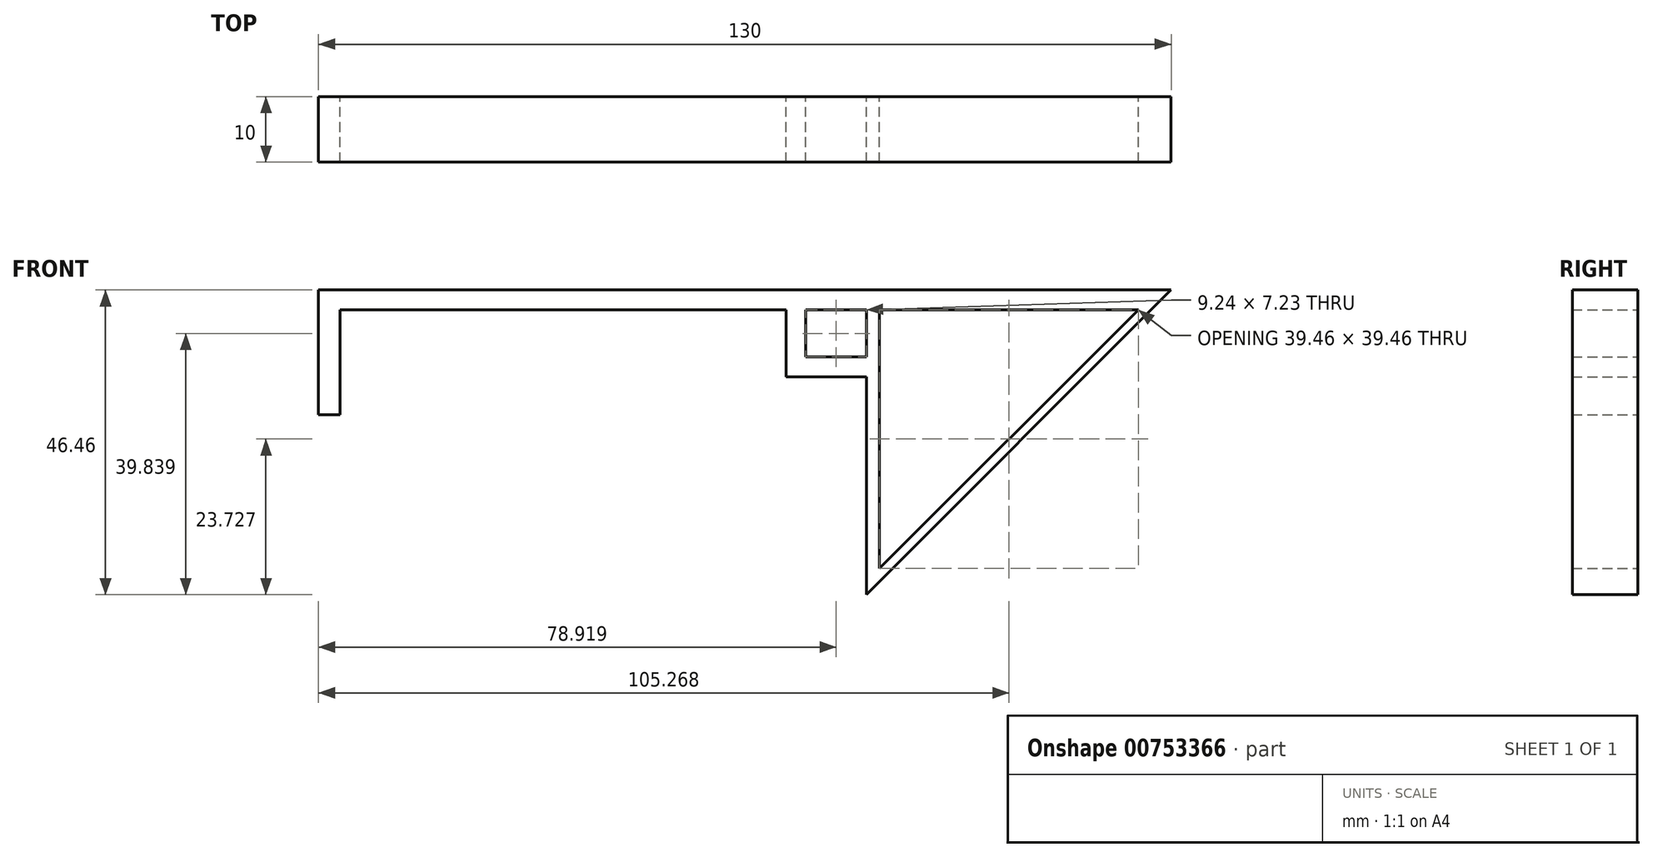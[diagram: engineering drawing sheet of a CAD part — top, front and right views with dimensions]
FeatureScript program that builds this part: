
annotation { "Feature Type Name" : "Feature", "Feature Type Description" : "" }
export const myFeature = defineFeature(function(context is Context, id is Id, definition is map)
    precondition{}
    {
        {
            var Q0;
            Q0=qCreatedBy(makeId("Front.planeOp"),FACE);
            var sketch = newSketch(context, id + "F0", { "sketchPlane" : qUnion([Q0])});
            skPoint(sketch, "E0", {"position": v(-32.18, 20.1) * mm});
            skPoint(sketch, "E1", {"position": v(-100.18, 20.1) * mm});
            skLineSegment(sketch, "E2", {"start": v(-100.18, 20.1) * mm, "end": v(-32.18, 20.1) * mm});
            skLineSegment(sketch, "E3", {"start": v(-100.18, 20.1) * mm, "end": v(-100.18, 4.1) * mm});
            skLineSegment(sketch, "E4", {"start": v(-100.18, 4.1) * mm, "end": v(-103.48, 4.1) * mm});
            skPoint(sketch, "E5", {"position": v(-103.48, 4.1) * mm});
            skLineSegment(sketch, "E6", {"start": v(-103.48, 4.1) * mm, "end": v(-103.48, 20.1) * mm});
            skLineSegment(sketch, "E7", {"start": v(-103.48, 20.1) * mm, "end": v(-103.48, 23.1) * mm});
            skLineSegment(sketch, "E8", {"start": v(-103.48, 23.1) * mm, "end": v(26.52, 23.1) * mm});
            skLineSegment(sketch, "E9", {"start": v(-32.18, 20.1) * mm, "end": v(-32.18, 9.87) * mm});
            skLineSegment(sketch, "E10", {"start": v(26.52, 23.1) * mm, "end": v(-14.52, -17.93) * mm});
            skLineSegment(sketch, "E11", {"start": v(-14.52, -17.93) * mm, "end": v(-19.94, -23.35) * mm});
            skLineSegment(sketch, "E12", {"start": v(-32.18, 9.87) * mm, "end": v(-19.94, 9.87) * mm});
            skLineSegment(sketch, "E13", {"start": v(-19.94, 9.87) * mm, "end": v(-19.94, -23.35) * mm});
            skLineSegment(sketch, "E14", {"start": v(-19.94, 9.87) * mm, "end": v(-19.94, 23.1) * mm});
            skPoint(sketch, "E15", {"position": v(-29.18, 9.87) * mm});
            skPoint(sketch, "E16", {"position": v(-22.94, 9.87) * mm});
            skLineSegment(sketch, "E17", {"start": v(-29.18, 9.87) * mm, "end": v(-29.18, 23.1) * mm});
            skPoint(sketch, "E18", {"position": v(-19.94, 12.87) * mm});
            skLineSegment(sketch, "E19", {"start": v(-19.94, 12.87) * mm, "end": v(-32.18, 12.87) * mm});
            skPoint(sketch, "E20", {"position": v(-17.94, 23.1) * mm});
            skPoint(sketch, "E21", {"position": v(24.52, 23.1) * mm});
            skLineSegment(sketch, "E22", {"start": v(24.52, 23.1) * mm, "end": v(-19.94, -21.35) * mm});
            skLineSegment(sketch, "E23", {"start": v(-17.94, 23.1) * mm, "end": v(-17.94, -19.35) * mm});
            skLineSegment(sketch, "E24", {"start": v(-32.18, 20.1) * mm, "end": v(23.52, 20.1) * mm});
            skSolve(sketch);
        }
        {
            var Q0;
            Q0 = qSketchRegion(id + "F0", true);
            extrude(context, id + "F1", {"entities" : qUnion([Q0]), "depth" : 10 * mm, "offsetDistance" : 25 * mm});
        }
    });
